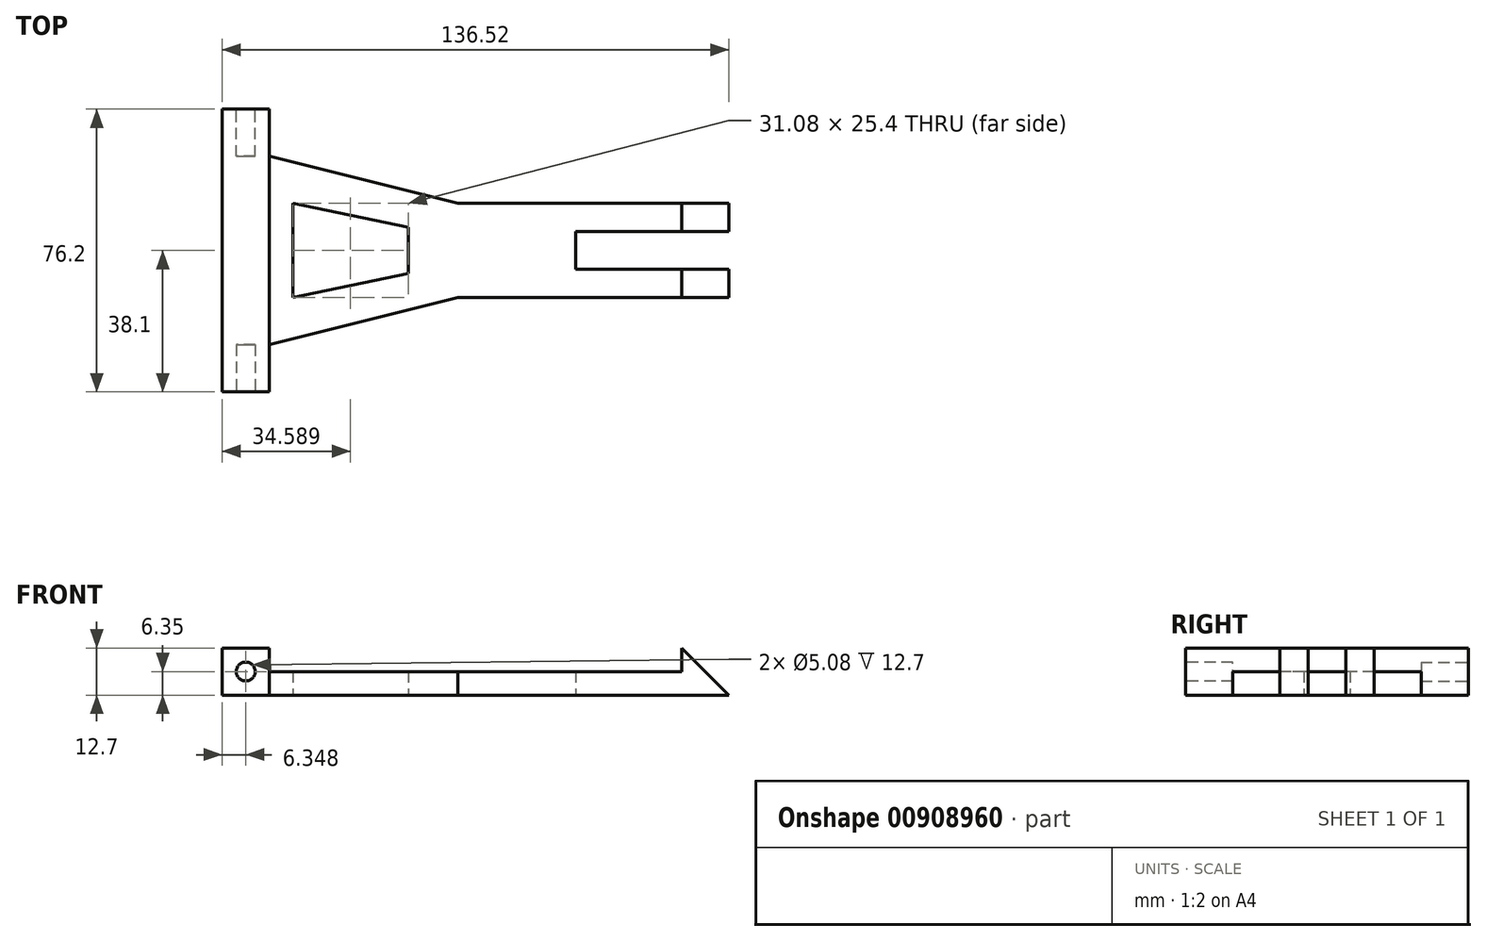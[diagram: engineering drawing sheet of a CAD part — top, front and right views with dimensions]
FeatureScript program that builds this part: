
annotation { "Feature Type Name" : "Feature", "Feature Type Description" : "" }
export const myFeature = defineFeature(function(context is Context, id is Id, definition is map)
    precondition{}
    {
        {
            var Q0;
            Q0=qCreatedBy(makeId("Top.planeOp"),FACE);
            var sketch = newSketch(context, id + "F0", { "sketchPlane" : qUnion([Q0])});
            skLineSegment(sketch, "E0.bottom", {"start": v(-68.26, -38.1) * mm, "end": v(68.26, -38.1) * mm});
            skLineSegment(sketch, "E0.top", {"start": v(-68.26, 38.1) * mm, "end": v(68.26, 38.1) * mm});
            skLineSegment(sketch, "E0.left", {"start": v(-68.26, -38.1) * mm, "end": v(-68.26, 38.1) * mm});
            skLineSegment(sketch, "E0.right", {"start": v(68.26, -38.1) * mm, "end": v(68.26, 38.1) * mm});
            skPoint(sketch, "E0.middle", {"position": v(0, 0) * mm});
            skLineSegment(sketch, "E1", {"start": v(-55.56, -38.1) * mm, "end": v(-55.56, -25.4) * mm});
            skLineSegment(sketch, "E2", {"start": v(-55.56, -25.4) * mm, "end": v(-4.76, -12.7) * mm});
            skLineSegment(sketch, "E3", {"start": v(-4.76, -12.7) * mm, "end": v(68.26, -12.7) * mm});
            skLineSegment(sketch, "E4.bottom", {"start": v(68.26, -5.08) * mm, "end": v(26.99, -5.08) * mm});
            skLineSegment(sketch, "E4.top", {"start": v(68.26, 5.08) * mm, "end": v(26.99, 5.08) * mm});
            skLineSegment(sketch, "E4.left", {"start": v(68.26, -5.08) * mm, "end": v(68.26, 5.08) * mm});
            skLineSegment(sketch, "E4.right", {"start": v(26.99, -5.08) * mm, "end": v(26.99, 5.08) * mm});
            skPoint(sketch, "E4.middle", {"position": v(47.62, 0) * mm});
            skLineSegment(sketch, "E5.MirrorCS", {"start": v(-55.56, 38.1) * mm, "end": v(-55.56, 25.4) * mm});
            skLineSegment(sketch, "E6.MirrorCS", {"start": v(-55.56, 25.4) * mm, "end": v(-4.76, 12.7) * mm});
            skLineSegment(sketch, "E7.MirrorCS", {"start": v(-4.76, 12.7) * mm, "end": v(68.26, 12.7) * mm});
            skLineSegment(sketch, "E8", {"start": v(-49.21, 12.7) * mm, "end": v(-18.13, 6.22) * mm});
            skLineSegment(sketch, "E9", {"start": v(-18.13, 6.22) * mm, "end": v(-18.13, -6.22) * mm});
            skLineSegment(sketch, "E10", {"start": v(-18.13, -6.22) * mm, "end": v(-49.21, -12.7) * mm});
            skLineSegment(sketch, "E11", {"start": v(-49.21, 12.7) * mm, "end": v(-49.21, -12.7) * mm});
            skSolve(sketch);
        }
        {
            var Q0;
            {var subQ7=sQuery(id+"F0.wireOp",EDGE,"E0.left");Q0=makeQuery(id+"F0.imprint","IMPRINT",FACE,{"disambiguationData":[TD([[makeQuery(id+"F0.imprint","IMPRINT",EDGE,{"derivedFrom":subQ7}),-1.0]])]});}
            extrude(context, id + "F1", {"entities" : qUnion([Q0]), "depth" : 12.7 * mm, "offsetDistance" : 25 * mm});
        }
        {
            var Q0;
            Q0=makeQuery(id+"F1.opExtrude","CAP_FACE",FACE,{"disambiguationData":[OSD([sQuery(id+"F0.wireOp",EDGE,"E0.bottom"),sQuery(id+"F0.wireOp",EDGE,"E0.top"),sQuery(id+"F0.wireOp",EDGE,"E0.left"),sQuery(id+"F0.wireOp",EDGE,"E0.right"),sQuery(id+"F0.wireOp",EDGE,"E1"),sQuery(id+"F0.wireOp",EDGE,"E2"),sQuery(id+"F0.wireOp",EDGE,"E3"),sQuery(id+"F0.wireOp",EDGE,"E4.bottom"),sQuery(id+"F0.wireOp",EDGE,"E4.top"),sQuery(id+"F0.wireOp",EDGE,"E4.right"),sQuery(id+"F0.wireOp",EDGE,"E5.MirrorCS"),sQuery(id+"F0.wireOp",EDGE,"E6.MirrorCS"),sQuery(id+"F0.wireOp",EDGE,"E7.MirrorCS"),sQuery(id+"F0.wireOp",EDGE,"E8"),sQuery(id+"F0.wireOp",EDGE,"E9"),sQuery(id+"F0.wireOp",EDGE,"E10"),sQuery(id+"F0.wireOp",EDGE,"E11")])],"isStart":false});
            var sketch = newSketch(context, id + "F2", { "sketchPlane" : qUnion([Q0])});
            skLineSegment(sketch, "E12.0", {"start": v(-68.26, -38.1) * mm, "end": v(68.26, -38.1) * mm});
            skLineSegment(sketch, "E12.1", {"start": v(-68.26, 38.1) * mm, "end": v(68.26, 38.1) * mm});
            skLineSegment(sketch, "E12.2", {"start": v(-68.26, -38.1) * mm, "end": v(-68.26, 38.1) * mm});
            skLineSegment(sketch, "E12.3", {"start": v(68.26, -38.1) * mm, "end": v(68.26, 38.1) * mm});
            skPoint(sketch, "E12.4", {"position": v(0, 0) * mm});
            skLineSegment(sketch, "E12.5", {"start": v(-55.56, -38.1) * mm, "end": v(-55.56, -25.4) * mm});
            skLineSegment(sketch, "E12.6", {"start": v(-55.56, -25.4) * mm, "end": v(-4.76, -12.7) * mm});
            skLineSegment(sketch, "E12.7", {"start": v(-4.76, -12.7) * mm, "end": v(68.26, -12.7) * mm});
            skLineSegment(sketch, "E12.8", {"start": v(68.26, -5.08) * mm, "end": v(26.99, -5.08) * mm});
            skLineSegment(sketch, "E12.9", {"start": v(68.26, 5.08) * mm, "end": v(26.99, 5.08) * mm});
            skLineSegment(sketch, "E12.10", {"start": v(68.26, -5.08) * mm, "end": v(68.26, 5.08) * mm});
            skLineSegment(sketch, "E12.11", {"start": v(26.99, -5.08) * mm, "end": v(26.99, 5.08) * mm});
            skPoint(sketch, "E12.12", {"position": v(47.62, 0) * mm});
            skLineSegment(sketch, "E12.13", {"start": v(-55.56, 38.1) * mm, "end": v(-55.56, 25.4) * mm});
            skLineSegment(sketch, "E12.14", {"start": v(-55.56, 25.4) * mm, "end": v(-4.76, 12.7) * mm});
            skLineSegment(sketch, "E12.15", {"start": v(-4.76, 12.7) * mm, "end": v(68.26, 12.7) * mm});
            skLineSegment(sketch, "E12.16", {"start": v(-49.21, 12.7) * mm, "end": v(-18.13, 6.22) * mm});
            skLineSegment(sketch, "E12.17", {"start": v(-18.13, 6.22) * mm, "end": v(-18.13, -6.22) * mm});
            skLineSegment(sketch, "E12.18", {"start": v(-18.13, -6.22) * mm, "end": v(-49.21, -12.7) * mm});
            skLineSegment(sketch, "E12.19", {"start": v(-49.21, 12.7) * mm, "end": v(-49.21, -12.7) * mm});
            skLineSegment(sketch, "E13", {"start": v(-55.56, 25.4) * mm, "end": v(-55.56, -25.4) * mm});
            skLineSegment(sketch, "E14", {"start": v(55.56, 12.7) * mm, "end": v(55.56, -12.7) * mm});
            skSolve(sketch);
        }
        {
            var Q0;
            {var subQ5=sQuery(id+"F2.wireOp",EDGE,"E12.6");Q0=makeQuery(id+"F2.imprint","IMPRINT",FACE,{"disambiguationData":[TD([[makeQuery(id+"F2.imprint","IMPRINT",EDGE,{"derivedFrom":subQ5}),1.0]])]});}
            extrude(context, id + "F3", {"entities" : qUnion([Q0]), "operationType" : NewBodyOperationType.REMOVE, "oppositeDirection" : true, "depth" : 6.35 * mm, "offsetDistance" : 25 * mm});
        }
        {
            var Q0;
            Q0=makeQuery(id+"F1.opExtrude","SWEPT_FACE",FACE,{"disambiguationData":[OSD([sQuery(id+"F0.wireOp",EDGE,"E0.bottom")])]});
            var sketch = newSketch(context, id + "F4", { "sketchPlane" : qUnion([Q0])});
            skLineSegment(sketch, "E15.0.0", {"start": v(-68.26, 0) * mm, "end": v(-55.56, 0) * mm});
            skLineSegment(sketch, "E15.0.1", {"start": v(-55.56, 0) * mm, "end": v(-55.56, 12.7) * mm});
            skLineSegment(sketch, "E15.0.2", {"start": v(-55.56, 12.7) * mm, "end": v(-68.26, 12.7) * mm});
            skLineSegment(sketch, "E15.0.3", {"start": v(-68.26, 12.7) * mm, "end": v(-68.26, 0) * mm});
            skLineSegment(sketch, "E16.0.0", {"start": v(55.56, 6.35) * mm, "end": v(-4.76, 6.35) * mm});
            skLineSegment(sketch, "E16.0.1", {"start": v(-4.76, 6.35) * mm, "end": v(-4.76, 0) * mm});
            skLineSegment(sketch, "E16.0.2", {"start": v(-4.76, 0) * mm, "end": v(68.26, 0) * mm});
            skLineSegment(sketch, "E16.0.3", {"start": v(68.26, 0) * mm, "end": v(68.26, 12.7) * mm});
            skLineSegment(sketch, "E16.0.4", {"start": v(68.26, 12.7) * mm, "end": v(55.56, 12.7) * mm});
            skLineSegment(sketch, "E16.0.5", {"start": v(55.56, 12.7) * mm, "end": v(55.56, 6.35) * mm});
            skLineSegment(sketch, "E17", {"start": v(-68.26, 0) * mm, "end": v(-55.56, 12.7) * mm, "construction": true});
            skLineSegment(sketch, "E18", {"start": v(-68.26, 12.7) * mm, "end": v(-55.56, 0) * mm, "construction": true});
            skLineSegment(sketch, "E19", {"start": v(55.56, 6.35) * mm, "end": v(55.56, 0) * mm, "construction": true});
            skLineSegment(sketch, "E20", {"start": v(55.56, 0) * mm, "end": v(68.26, 12.7) * mm, "construction": true});
            skLineSegment(sketch, "E21", {"start": v(55.56, 12.7) * mm, "end": v(68.26, 0) * mm, "construction": true});
            skCircle(sketch, "E22", {"center": v(61.91, 6.35) * mm, "radius": 2.54 * mm});
            skCircle(sketch, "E23", {"center": v(-61.91, 6.35) * mm, "radius": 2.54 * mm});
            skSolve(sketch);
        }
        {
            var Q0;
            Q0=makeQuery(id+"F4.imprint","IMPRINT",FACE,{"disambiguationData":[TD([[makeQuery(id+"F4.imprint","IMPRINT",EDGE,{"derivedFrom":sQuery(id+"F4.wireOp",EDGE,"E23")}),1.0]])]});
            extrude(context, id + "F5", {"entities" : qUnion([Q0]), "operationType" : NewBodyOperationType.REMOVE, "oppositeDirection" : true, "depth" : 12.7 * mm, "offsetDistance" : 25 * mm});
        }
        {
            var Q0;
            Q0=makeQuery(id+"F1.opExtrude","SWEPT_FACE",FACE,{"disambiguationData":[OSD([sQuery(id+"F0.wireOp",EDGE,"E0.bottom")])]});
            var sketch = newSketch(context, id + "F6", { "sketchPlane" : qUnion([Q0])});
            skLineSegment(sketch, "E24.0", {"start": v(-68.26, 0) * mm, "end": v(-55.56, 0) * mm});
            skLineSegment(sketch, "E24.1", {"start": v(-55.56, 0) * mm, "end": v(-55.56, 12.7) * mm});
            skLineSegment(sketch, "E24.2", {"start": v(-55.56, 12.7) * mm, "end": v(-68.26, 12.7) * mm});
            skLineSegment(sketch, "E24.3", {"start": v(-68.26, 12.7) * mm, "end": v(-68.26, 0) * mm});
            skLineSegment(sketch, "E24.4", {"start": v(55.56, 6.35) * mm, "end": v(-4.76, 6.35) * mm});
            skLineSegment(sketch, "E24.5", {"start": v(-4.76, 6.35) * mm, "end": v(-4.76, 0) * mm});
            skLineSegment(sketch, "E24.6", {"start": v(-4.76, 0) * mm, "end": v(68.26, 0) * mm});
            skLineSegment(sketch, "E24.7", {"start": v(68.26, 0) * mm, "end": v(68.26, 12.7) * mm});
            skLineSegment(sketch, "E24.8", {"start": v(68.26, 12.7) * mm, "end": v(55.56, 12.7) * mm});
            skLineSegment(sketch, "E24.9", {"start": v(55.56, 12.7) * mm, "end": v(55.56, 6.35) * mm});
            skLineSegment(sketch, "E24.10", {"start": v(-68.26, 0) * mm, "end": v(-55.56, 12.7) * mm});
            skLineSegment(sketch, "E24.11", {"start": v(-68.26, 12.7) * mm, "end": v(-55.56, 0) * mm});
            skLineSegment(sketch, "E24.12", {"start": v(55.56, 6.35) * mm, "end": v(55.56, 0) * mm});
            skLineSegment(sketch, "E24.13", {"start": v(55.56, 0) * mm, "end": v(68.26, 12.7) * mm});
            skLineSegment(sketch, "E24.14", {"start": v(55.56, 12.7) * mm, "end": v(68.26, 0) * mm});
            skCircle(sketch, "E24.15", {"center": v(61.91, 6.35) * mm, "radius": 2.54 * mm});
            skCircle(sketch, "E24.16", {"center": v(-61.91, 6.35) * mm, "radius": 2.54 * mm});
            skSolve(sketch);
        }
        {
            var Q0;
            {var subQ0=sQuery(id+"F6.wireOp",EDGE,"E24.15");var subQ1=sQuery(id+"F6.wireOp",EDGE,"E24.13");var subQ2=makeQuery(id+"F6.imprint","INTERSECT",VERTEX,{"disambiguationData":[OD(0.0)],"derivedFrom":[subQ1,subQ0]});Q0=makeQuery(id+"F6.imprint","IMPRINT",FACE,{"disambiguationData":[TD([[makeQuery(id+"F6.imprint","IMPRINT",EDGE,{"disambiguationData":[TD([[subQ2,-1.0]])],"derivedFrom":subQ1}),-1.0]])]});}
            var Q1;
            {var subQ0=sQuery(id+"F6.wireOp",EDGE,"E24.15");var subQ1=sQuery(id+"F6.wireOp",EDGE,"E24.13");var subQ2=makeQuery(id+"F6.imprint","INTERSECT",VERTEX,{"disambiguationData":[OD(0.0)],"derivedFrom":[subQ1,subQ0]});Q1=makeQuery(id+"F6.imprint","IMPRINT",FACE,{"disambiguationData":[TD([[makeQuery(id+"F6.imprint","IMPRINT",EDGE,{"disambiguationData":[TD([[subQ2,-1.0]])],"derivedFrom":subQ1}),1.0]])]});}
            var Q2;
            {var subQ0=sQuery(id+"F6.wireOp",EDGE,"E24.14");var subQ1=sQuery(id+"F6.wireOp",EDGE,"E24.13");var subQ2=makeQuery(id+"F6.imprint","INTERSECT",VERTEX,{"derivedFrom":[subQ1,subQ0]});Q2=makeQuery(id+"F6.imprint","IMPRINT",FACE,{"disambiguationData":[TD([[makeQuery(id+"F6.imprint","IMPRINT",EDGE,{"disambiguationData":[TD([[subQ2,-1.0]])],"derivedFrom":subQ1}),1.0]])]});}
            var Q3;
            {var subQ0=sQuery(id+"F6.wireOp",EDGE,"E24.14");var subQ1=sQuery(id+"F6.wireOp",EDGE,"E24.13");var subQ2=makeQuery(id+"F6.imprint","INTERSECT",VERTEX,{"derivedFrom":[subQ1,subQ0]});Q3=makeQuery(id+"F6.imprint","IMPRINT",FACE,{"disambiguationData":[TD([[makeQuery(id+"F6.imprint","IMPRINT",EDGE,{"disambiguationData":[TD([[subQ2,-1.0]])],"derivedFrom":subQ1}),-1.0]])]});}
            extrude(context, id + "F7", {"entities" : qUnion([Q0, Q1, Q2, Q3]), "operationType" : NewBodyOperationType.REMOVE, "endBound" : BoundingType.THROUGH_ALL, "oppositeDirection" : true, "depth" : 25 * mm, "offsetDistance" : 25 * mm});
        }
        {
            var Q0;
            Q0=makeQuery(id+"F1.opExtrude","SWEPT_FACE",FACE,{"disambiguationData":[OSD([sQuery(id+"F0.wireOp",EDGE,"E0.top")])]});
            var sketch = newSketch(context, id + "F8", { "sketchPlane" : qUnion([Q0])});
            skLineSegment(sketch, "E25", {"start": v(68.26, 12.7) * mm, "end": v(55.56, 0) * mm, "construction": true});
            skLineSegment(sketch, "E26", {"start": v(68.26, 0) * mm, "end": v(55.56, 12.7) * mm, "construction": true});
            skCircle(sketch, "E27", {"center": v(61.91, 6.35) * mm, "radius": 2.54 * mm});
            skSolve(sketch);
        }
        {
            var Q0;
            Q0=makeQuery(id+"F8.imprint","IMPRINT",FACE,{"disambiguationData":[TD([[makeQuery(id+"F8.imprint","IMPRINT",EDGE,{"derivedFrom":sQuery(id+"F8.wireOp",EDGE,"E27")}),1.0]])]});
            extrude(context, id + "F9", {"entities" : qUnion([Q0]), "operationType" : NewBodyOperationType.REMOVE, "oppositeDirection" : true, "depth" : 12.7 * mm, "offsetDistance" : 25 * mm});
        }
    });
